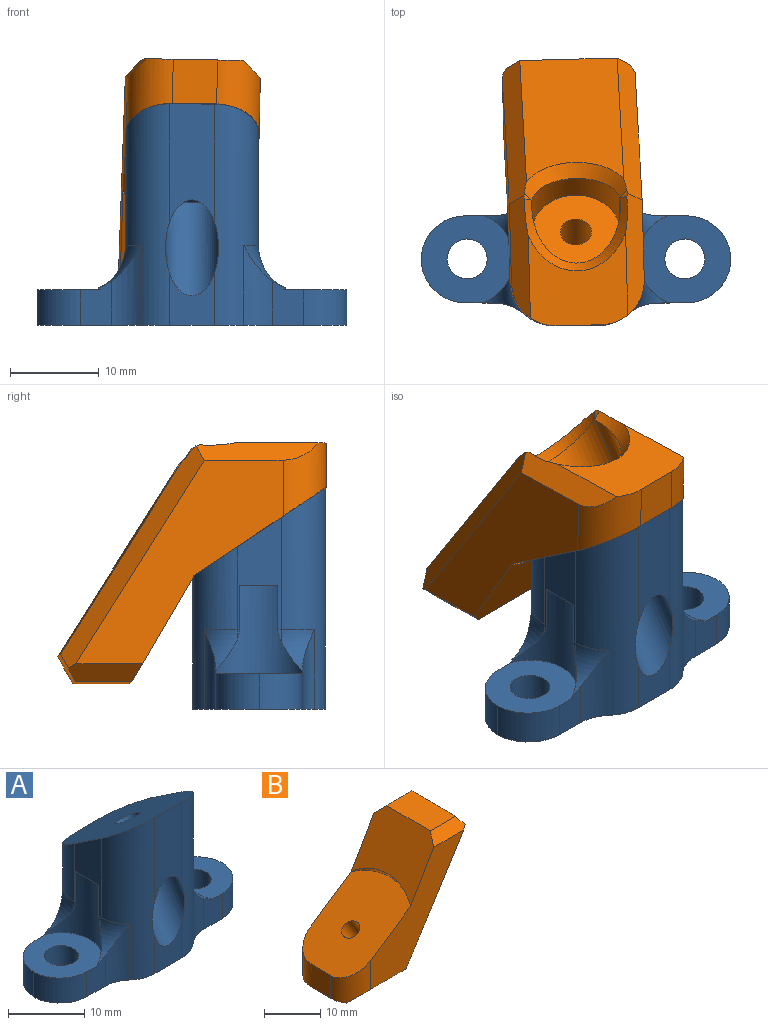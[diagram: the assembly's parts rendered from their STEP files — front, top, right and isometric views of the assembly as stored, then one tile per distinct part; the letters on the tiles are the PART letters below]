
ASSEMBLY  parts=2 mates=1
PART A: 42 faces, bbox 35x23.1x25 mm
  f0: plane 35x15mm, normal (0,0,-1), area 351.3mm2, adj f2,f3,f8,f13,f14,f15,f17,f18
  f1: plane 13.26x5mm, normal (0,-1,0), area 57.8mm2, adj f9,f11,f13,f30
  f2: plane 15x5mm, normal (0,1,0), area 75mm2, adj f0,f8,f9,f29
  f3: plane 5.76x5mm, normal (0,-1,0), area 20.3mm2, adj f0,f11,f13,f30
  f4: torus R=10mm, axis (0,0,-1), area 12mm2, adj f5,f13,f15,f18,f23
  f5: cylinder r=5mm len=1.4mm, axis (0,-1,0), area 0.4mm2, adj f4,f7,f23
  f6: torus R=10mm, axis (0,0,-1), area 11.6mm2, adj f8,f14,f19,f20,f23
  f7: plane 12.67x5mm, normal (1,0,0), area 33.4mm2, adj f5,f8,f9,f13,f20,f23,f24
  f8: cylinder r=5mm len=18.33mm, axis (0,0,-1), area 89.6mm2, adj f0,f2,f6,f7,f9,f19
  f9: plane 15x15mm, normal (0,0.55,0.83), area 235mm2, adj f1,f2,f7,f8,f10,f13,f28,f29
  f10: cylinder r=1.75mm len=6.43mm, axis (0,0.55,0.83), area 59.4mm2, adj f9,f12
  f11: cylinder r=3mm len=13.83mm, axis (0,-0.55,-0.83), area 152.9mm2, adj f1,f3,f12,f13,f30
  f12: plane 6x4.99mm, normal (0,-0.55,-0.83), area 18.7mm2, adj f10,f11
  f13: cylinder r=5mm len=25mm, axis (0,0,1), area 147.1mm2, adj f0,f1,f3,f4,f7,f9,f11,f18
  f14: plane 4.97x3.43mm, normal (0.01,1,0), area 14.4mm2, adj f0,f6,f16,f19,f22,f23
  f15: plane 4.97x3.43mm, normal (0.01,-1,0), area 14.4mm2, adj f0,f4,f16,f18,f21,f23
  f16: plane 10.46x9.85mm, normal (0,0,1), area 66.9mm2, adj f14,f15,f17,f21,f22,f23
  f17: cylinder r=2.25mm len=4.5mm, axis (0,0,1), area 56.5mm2, adj f0,f16
  f18: cylinder r=5mm len=9mm, axis (0,0,1), area 24.3mm2, adj f0,f4,f13,f15
  f19: cylinder r=5mm len=9mm, axis (0,0,-1), area 24.3mm2, adj f0,f6,f8,f14
  f20: cylinder r=5mm len=1.19mm, axis (0,-1,0), area 0.2mm2, adj f6,f7,f23
  f21: cylinder r=5mm len=4.95mm, axis (0,0,-1), area 30.8mm2, adj f0,f15,f16,f22
  f22: cylinder r=5mm len=4.95mm, axis (0,0,1), area 30.8mm2, adj f0,f14,f16,f21
  f23: cylinder r=5.25mm len=10mm, axis (0,0,1), area 59.7mm2, adj f4,f5,f6,f7,f14,f15,f16,f20
  f24: plane 4.31x0.46mm, normal (0,0,-1), area 1.3mm2, adj f7,f23
  f25: torus R=10mm, axis (0,0,-1), area 12mm2, adj f26,f30,f32,f35,f40
  f26: cylinder r=5mm len=1.4mm, axis (0,-1,0), area 0.4mm2, adj f25,f28,f40
  f27: torus R=10mm, axis (0,0,-1), area 11.6mm2, adj f29,f31,f36,f37,f40
  f28: plane 12.67x5mm, normal (-1,0,0), area 33.4mm2, adj f9,f26,f29,f30,f37,f40,f41
  f29: cylinder r=5mm len=18.33mm, axis (0,0,-1), area 89.6mm2, adj f0,f2,f9,f27,f28,f36
  f30: cylinder r=5mm len=25mm, axis (0,0,1), area 147.1mm2, adj f0,f1,f3,f9,f11,f25,f28,f35
  f31: plane 4.97x3.43mm, normal (-0.01,1,0), area 14.4mm2, adj f0,f27,f33,f36,f39,f40
  f32: plane 4.97x3.43mm, normal (-0.01,-1,0), area 14.4mm2, adj f0,f25,f33,f35,f38,f40
  f33: plane 10.46x9.85mm, normal (0,0,1), area 66.9mm2, adj f31,f32,f34,f38,f39,f40
  f34: cylinder r=2.25mm len=4.5mm, axis (0,0,1), area 56.5mm2, adj f0,f33
  f35: cylinder r=5mm len=9mm, axis (0,0,1), area 24.3mm2, adj f0,f25,f30,f32
  f36: cylinder r=5mm len=9mm, axis (0,0,-1), area 24.3mm2, adj f0,f27,f29,f31
  f37: cylinder r=5mm len=1.19mm, axis (0,-1,0), area 0.2mm2, adj f27,f28,f40
  f38: cylinder r=5mm len=4.95mm, axis (0,0,-1), area 30.8mm2, adj f0,f32,f33,f39
  f39: cylinder r=5mm len=4.95mm, axis (0,0,1), area 30.8mm2, adj f0,f31,f33,f38
  f40: cylinder r=5.25mm len=10mm, axis (0,0,1), area 59.7mm2, adj f25,f26,f27,f28,f31,f32,f33,f37
  f41: plane 4.31x0.46mm, normal (0,0,-1), area 1.3mm2, adj f28,f40
PART B: 25 faces, bbox 31.5x16.4x30.5 mm
  f0: plane 23.4x23mm, normal (0,-1,0), area 208.8mm2, adj f4,f7,f9,f16,f17,f20,f24
  f1: plane 23.4x23mm, normal (0,1,0), area 208.8mm2, adj f4,f7,f9,f18,f19,f21,f23
  f2: plane 5x5mm, normal (-1,0,0), area 25mm2, adj f3,f4,f23,f24
  f3: plane 11.14x10.41mm, normal (0,0,-1), area 78.6mm2, adj f2,f14,f16,f18,f23,f24
  f4: plane 18.75x16.4mm, normal (-0.55,0,0.83), area 277.6mm2, adj f0,f1,f2,f5,f9,f23,f24
  f5: cylinder r=1.75mm len=6.52mm, axis (-0.55,0,0.83), area 60.5mm2, adj f4,f11
  f6: plane 21.83x13.79mm, normal (0.85,0,-0.53), area 252.9mm2, adj f13,f17,f19,f22
  f7: plane 15x11.86mm, normal (-0.86,0,0.51), area 170.9mm2, adj f0,f1,f8,f9,f20,f21
  f8: plane 11x6.37mm, normal (0,0,1), area 70.1mm2, adj f7,f20,f21,f22
  f9: cylinder r=11.84mm len=15mm, axis (-0.55,0,0.83), area 15.2mm2, adj f0,f1,f4,f7
  f10: cylinder r=5mm len=11.51mm, axis (0.55,0,-0.83), area 82.3mm2, adj f11,f13,f14
  f11: plane 10x8.32mm, normal (0.55,0,-0.83), area 68.9mm2, adj f5,f10
  f12: plane 0.92x0.79mm, normal (0.36,-0.66,-0.66), area 0.5mm2, adj f13,f14,f18,f19
  f13: bspline ~12.06x4.89mm, area 28.2mm2, adj f6,f10,f12,f15,f17,f19
  f14: bspline ~12.16x8.26mm, area 72.8mm2, adj f3,f10,f12,f15,f16,f18
  f15: plane 0.91x0.79mm, normal (0.36,0.66,-0.66), area 0.5mm2, adj f13,f14,f16,f17
  f16: plane 14.74x2.95mm, normal (0,-0.71,-0.71), area 33.1mm2, adj f0,f3,f14,f15,f17,f24
  f17: plane 25.19x16.29mm, normal (0.6,-0.71,-0.38), area 79mm2, adj f0,f6,f13,f15,f16,f20,f22
  f18: plane 14.74x2.95mm, normal (0,0.71,-0.71), area 33.1mm2, adj f1,f3,f12,f14,f19,f23
  f19: plane 25.19x16.29mm, normal (0.6,0.71,-0.38), area 79mm2, adj f1,f6,f12,f13,f18,f21,f22
  f20: plane 8.39x2mm, normal (0,-0.71,0.71), area 20.9mm2, adj f0,f7,f8,f17,f22
  f21: plane 8.39x2mm, normal (0,0.71,0.71), area 20.9mm2, adj f1,f7,f8,f19,f22
  f22: plane 14.07x3.07mm, normal (0.88,0,0.48), area 43.9mm2, adj f6,f8,f17,f19,f20,f21
  f23: cylinder r=5mm len=8.33mm, axis (0,0,-1), area 47.7mm2, adj f1,f2,f3,f4,f18
  f24: cylinder r=5mm len=8.33mm, axis (0,0,1), area 47.7mm2, adj f0,f2,f3,f4,f16
PLACE A t=(-1.62,16.2,0.46)mm fixed
PLACE B rot(axis=(-0.7,-0.72,0.01),179.3deg) t=(13.76,1.41,30.32)mm
MATE revolute A.f10 <-> B.f5  axis (0,0.55,0.83) through (5.88,8.7,20.46)mm
